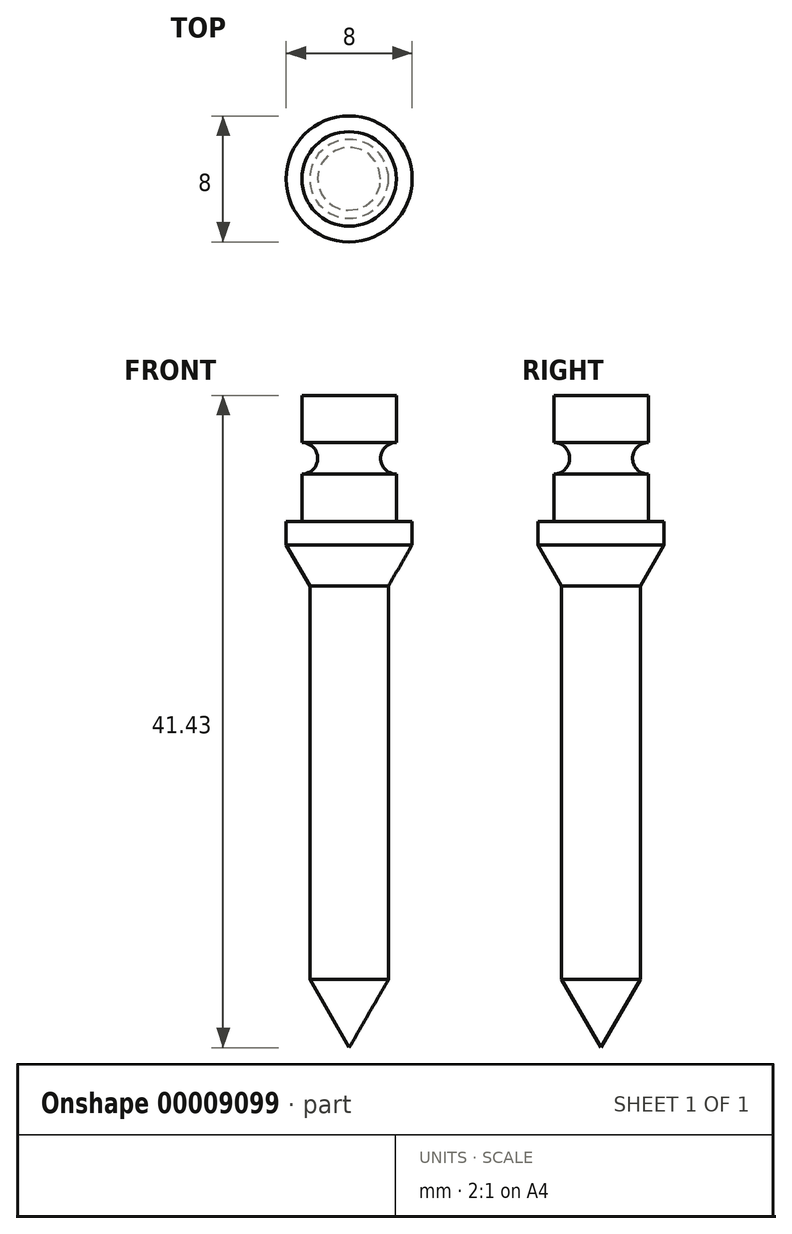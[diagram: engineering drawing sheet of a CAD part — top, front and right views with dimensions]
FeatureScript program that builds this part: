
annotation { "Feature Type Name" : "Feature", "Feature Type Description" : "" }
export const myFeature = defineFeature(function(context is Context, id is Id, definition is map)
    precondition{}
    {
        {
            var Q0;
            Q0=qCreatedBy(makeId("Front.planeOp"),FACE);
            var sketch = newSketch(context, id + "F0", { "sketchPlane" : qUnion([Q0])});
            skLineSegment(sketch, "E0", {"start": v(0, 0) * mm, "end": v(0, -43.36) * mm, "construction": true});
            skLineSegment(sketch, "E1", {"start": v(0, 0) * mm, "end": v(3, 0) * mm});
            skLineSegment(sketch, "E2", {"start": v(4, -9.5) * mm, "end": v(2.5, -12.1) * mm});
            skLineSegment(sketch, "E3", {"start": v(2.5, -12.1) * mm, "end": v(2.5, -37.1) * mm});
            skLineSegment(sketch, "E4", {"start": v(2.5, -37.1) * mm, "end": v(0, -41.43) * mm});
            skLineSegment(sketch, "E5", {"start": v(0, -41.43) * mm, "end": v(0, 0) * mm});
            skLineSegment(sketch, "E6", {"start": v(3, 0) * mm, "end": v(3, -8) * mm});
            skLineSegment(sketch, "E7", {"start": v(3, -8) * mm, "end": v(4, -8) * mm});
            skLineSegment(sketch, "E8", {"start": v(4, -8) * mm, "end": v(4, -9.5) * mm});
            skCircle(sketch, "E9", {"center": v(3, -4) * mm, "radius": 1 * mm});
            skSolve(sketch);
        }
        {
            var Q0;
            Q0=makeQuery(id+"F0.imprint","IMPRINT",FACE,{"disambiguationData":[TD([[makeQuery(id+"F0.imprint","IMPRINT",EDGE,{"derivedFrom":sQuery(id+"F0.wireOp",EDGE,"E1")}),-1.0]])]});
            var Q1;
            Q1=sQuery(id+"F0.wireOp",EDGE,"E0");
            revolve(context, id + "F1", {"entities" : qUnion([Q0]), "axis" : qUnion([Q1]), "revolveType" : RevolveType.FULL});
        }
    });
